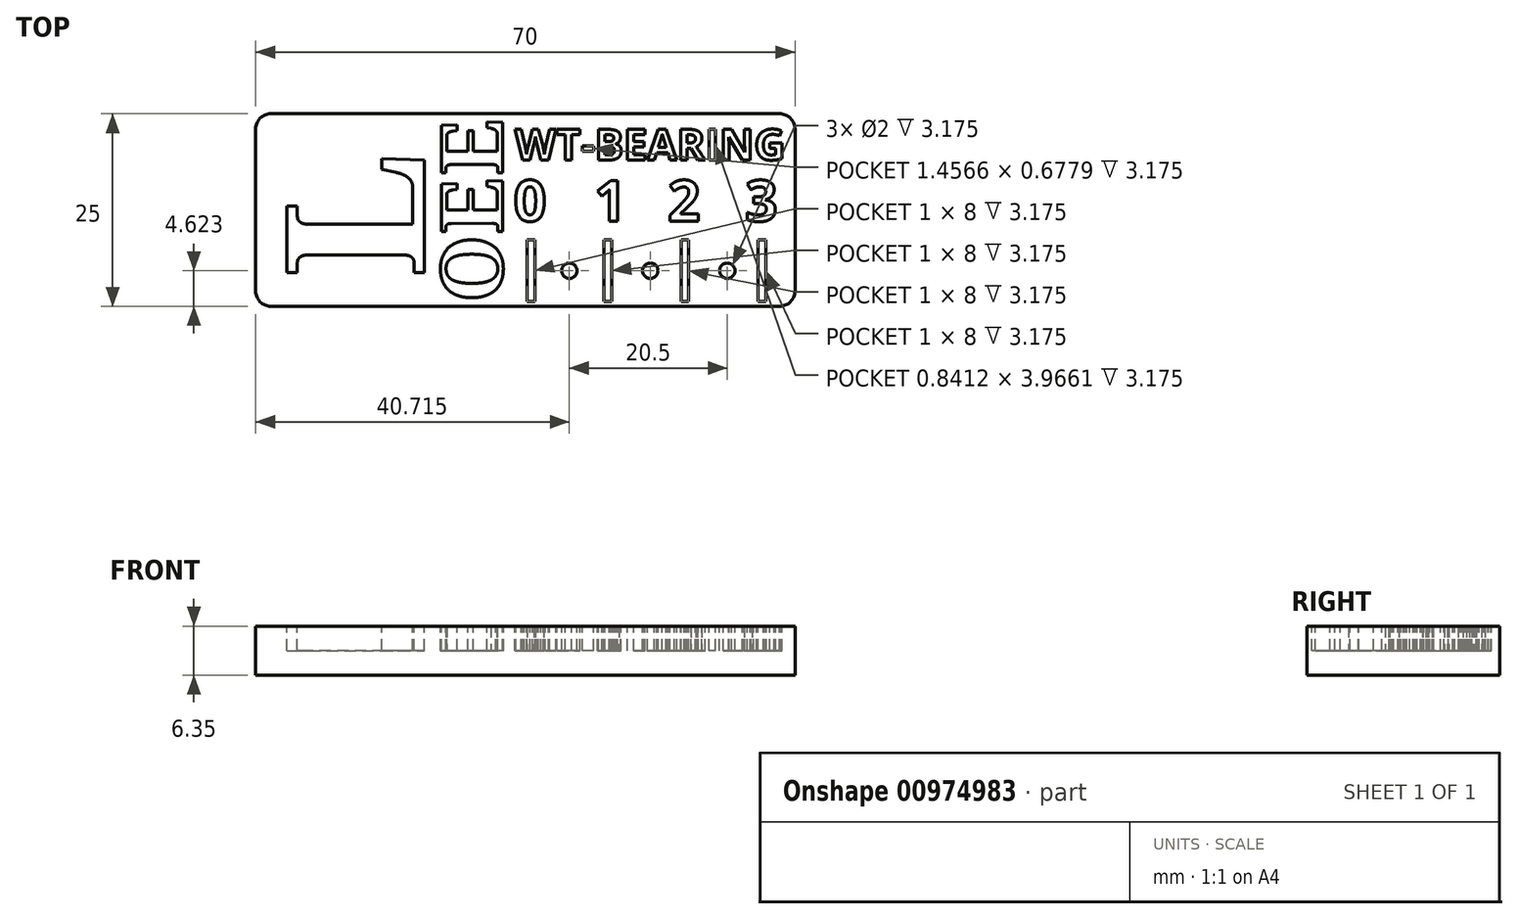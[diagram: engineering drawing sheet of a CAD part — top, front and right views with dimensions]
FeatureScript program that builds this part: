
annotation { "Feature Type Name" : "Feature", "Feature Type Description" : "" }
export const myFeature = defineFeature(function(context is Context, id is Id, definition is map)
    precondition{}
    {
        {
            var Q0;
            Q0=qCreatedBy(makeId("Top.planeOp"),FACE);
            var sketch = newSketch(context, id + "F0", { "sketchPlane" : qUnion([Q0])});
            skLineSegment(sketch, "E0.bottom", {"start": v(-55.27, 9.73) * mm, "end": v(10.73, 9.73) * mm});
            skLineSegment(sketch, "E0.top", {"start": v(-55.27, -15.27) * mm, "end": v(10.73, -15.27) * mm});
            skLineSegment(sketch, "E0.left", {"start": v(-57.27, 7.73) * mm, "end": v(-57.27, -13.27) * mm});
            skLineSegment(sketch, "E0.right", {"start": v(12.73, 7.73) * mm, "end": v(12.73, -13.27) * mm});
            skPoint(sketch, "E1.visualSharp", {"position": v(-57.27, 9.73) * mm});
            skArc(sketch, "E1.filletArc", {"start": v(-55.27, 9.73) * mm, "mid": v(-56.68, 9.15) * mm, "end": v(-57.27, 7.73) * mm});
            skPoint(sketch, "E2.visualSharp", {"position": v(12.73, 9.73) * mm});
            skArc(sketch, "E2.filletArc", {"start": v(12.73, 7.73) * mm, "mid": v(12.14, 9.15) * mm, "end": v(10.73, 9.73) * mm});
            skPoint(sketch, "E3.visualSharp", {"position": v(12.73, -15.27) * mm});
            skArc(sketch, "E3.filletArc", {"start": v(10.73, -15.27) * mm, "mid": v(12.14, -14.68) * mm, "end": v(12.73, -13.27) * mm});
            skPoint(sketch, "E4.visualSharp", {"position": v(-57.27, -15.27) * mm});
            skArc(sketch, "E4.filletArc", {"start": v(-57.27, -13.27) * mm, "mid": v(-56.68, -14.68) * mm, "end": v(-55.27, -15.27) * mm});
            skSolve(sketch);
        }
        {
            var Q0;
            Q0=qSketchRegion(id+"F0",true);
            extrude(context, id + "F1", {"entities" : qUnion([Q0]), "depth" : 6.35 * mm, "offsetDistance" : 25.4 * mm});
        }
        {
            var Q0;
            Q0=makeQuery(id+"F1.opExtrude","CAP_FACE",FACE,{"disambiguationData":[OSD([sQuery(id+"F0.wireOp",EDGE,"E0.bottom"),sQuery(id+"F0.wireOp",EDGE,"E0.top"),sQuery(id+"F0.wireOp",EDGE,"E0.left"),sQuery(id+"F0.wireOp",EDGE,"E0.right")])],"isStart":false});
            var sketch = newSketch(context, id + "F2", { "sketchPlane" : qUnion([Q0])});
            skText(sketch, "E5", { "text": "L", "fontName": "NotoSerif-Bold.ttf"});
            skText(sketch, "E6", { "text": "O\n", "fontName": "NotoSerif-Bold.ttf"});
            skText(sketch, "E7", { "text": "E", "fontName": "NotoSerif-Bold.ttf"});
            skLineSegment(sketch, "E8.bottom", {"start": v(-22.06, -6.65) * mm, "end": v(-21.06, -6.65) * mm});
            skLineSegment(sketch, "E8.top", {"start": v(-22.06, -14.65) * mm, "end": v(-21.06, -14.65) * mm});
            skLineSegment(sketch, "E8.left", {"start": v(-22.06, -6.65) * mm, "end": v(-22.06, -14.65) * mm});
            skLineSegment(sketch, "E8.right", {"start": v(-21.06, -6.65) * mm, "end": v(-21.06, -14.65) * mm});
            skLineSegment(sketch, "E9.bottom", {"start": v(-12.06, -6.65) * mm, "end": v(-11.06, -6.65) * mm});
            skLineSegment(sketch, "E9.top", {"start": v(-12.06, -14.65) * mm, "end": v(-11.06, -14.65) * mm});
            skLineSegment(sketch, "E9.left", {"start": v(-12.06, -6.65) * mm, "end": v(-12.06, -14.65) * mm});
            skLineSegment(sketch, "E9.right", {"start": v(-11.06, -6.65) * mm, "end": v(-11.06, -14.65) * mm});
            skLineSegment(sketch, "E10.bottom", {"start": v(-2.06, -6.65) * mm, "end": v(-1.06, -6.65) * mm});
            skLineSegment(sketch, "E10.top", {"start": v(-2.06, -14.65) * mm, "end": v(-1.06, -14.65) * mm});
            skLineSegment(sketch, "E10.left", {"start": v(-2.06, -6.65) * mm, "end": v(-2.06, -14.65) * mm});
            skLineSegment(sketch, "E10.right", {"start": v(-1.06, -6.65) * mm, "end": v(-1.06, -14.65) * mm});
            skLineSegment(sketch, "E11.bottom", {"start": v(7.94, -6.65) * mm, "end": v(8.94, -6.65) * mm});
            skLineSegment(sketch, "E11.top", {"start": v(7.94, -14.65) * mm, "end": v(8.94, -14.65) * mm});
            skLineSegment(sketch, "E11.left", {"start": v(7.94, -6.65) * mm, "end": v(7.94, -14.65) * mm});
            skLineSegment(sketch, "E11.right", {"start": v(8.94, -6.65) * mm, "end": v(8.94, -14.65) * mm});
            skPoint(sketch, "E12", {"position": v(-21.56, -6.65) * mm});
            skPoint(sketch, "E13", {"position": v(-11.56, -6.65) * mm});
            skPoint(sketch, "E14", {"position": v(-1.56, -6.65) * mm});
            skCircle(sketch, "E15", {"center": v(-16.56, -10.65) * mm, "radius": 1 * mm});
            skPoint(sketch, "E16", {"position": v(-21.06, -10.65) * mm});
            skCircle(sketch, "E17", {"center": v(-6.06, -10.65) * mm, "radius": 1 * mm});
            skCircle(sketch, "E18", {"center": v(3.94, -10.65) * mm, "radius": 1 * mm});
            skPoint(sketch, "E19", {"position": v(-11.06, -10.65) * mm});
            skPoint(sketch, "E20", {"position": v(-1.06, -10.65) * mm});
            skText(sketch, "E21", { "text": "0", "fontName": "OpenSans-Bold.ttf"});
            skText(sketch, "E22", { "text": "1", "fontName": "OpenSans-Bold.ttf"});
            skText(sketch, "E23", { "text": "2", "fontName": "OpenSans-Bold.ttf"});
            skText(sketch, "E24", { "text": "3", "fontName": "OpenSans-Bold.ttf"});
            skLineSegment(sketch, "E25", {"start": v(-39.23, 23.36) * mm, "end": v(-48.9, 23.36) * mm});
            skLineSegment(sketch, "E26", {"start": v(-48.9, 23.36) * mm, "end": v(-48.9, 20.36) * mm});
            skLineSegment(sketch, "E27", {"start": v(-48.9, 20.36) * mm, "end": v(-53.2, 24.99) * mm});
            skLineSegment(sketch, "E28", {"start": v(-53.2, 24.99) * mm, "end": v(-48.9, 28.97) * mm});
            skLineSegment(sketch, "E29", {"start": v(-48.9, 28.97) * mm, "end": v(-48.9, 25.97) * mm});
            skLineSegment(sketch, "E30", {"start": v(-48.9, 25.97) * mm, "end": v(-39.23, 25.97) * mm});
            skPoint(sketch, "E31", {"position": v(-41.72, 24.66) * mm});
            skLineSegment(sketch, "E32", {"start": v(-41.72, 24.66) * mm, "end": v(-39.23, 23.36) * mm});
            skLineSegment(sketch, "E33", {"start": v(-41.72, 24.66) * mm, "end": v(-39.23, 25.97) * mm});
            skText(sketch, "E34", { "text": "E", "fontName": "NotoSerif-Bold.ttf"});
            skText(sketch, "E35", { "text": "WT-BEARING", "fontName": "OpenSans-Bold.ttf"});
            const initialGuessF2  = {"E5": [-0.03535, -0.01161, 0, 1, 0.018], "E6": [-0.02523, -0.01477, 0, 1, 0.008], "E7": [-0.02523, -0.00585, -0.00042, 1, 0.008], "E21": [-0.02378, -0.00422, 1, 0, 0.00534], "E22": [-0.01333, -0.00422, 1, 0, 0.00534], "E23": [-0.0038, -0.00422, 1, 0, 0.00534], "E24": [0.00623, -0.00422, 1, 0, 0.00534], "E34": [-0.02523, 0.00178, -0.00042, 1, 0.008], "E35": [-0.02364, 0.00373, 1, 0, 0.004]};
            skSetInitialGuess(sketch, initialGuessF2);
            skSolve(sketch);
        }
        {
            var Q0;
            Q0=qSketchRegion(id+"F2",true);
            extrude(context, id + "F3", {"entities" : qUnion([Q0]), "operationType" : NewBodyOperationType.REMOVE, "oppositeDirection" : true, "depth" : 3.17 * mm, "offsetDistance" : 25.4 * mm});
        }
    });
